# Revit family: ContinuousSpouting_RainwaterHead_Taper
name_source: partatom
category: Plumbing Fixtures
revit_build: Autodesk Revit 2013 (Build: 20121003_2115(x64)
units: mm (PartAtom-declared; Revit-internal decimal feet)

## types (5) — shared parameters
Base Depth = 155 mm  [stored 0.50853 ft]
Base Width = 200 mm  [stored 0.656168 ft]
Distance from Wall = 20 mm  [stored 0.0656168 ft]
Downpipe Offset = 100 mm  [stored 0.328084 ft]
Downpipe Radius = 40 mm  [stored 0.131234 ft]
Height = 300 mm  [stored 0.984252 ft]
Hole Radius = 39 mm  [stored 0.127953 ft]
Manufacturer = Continuous Group NZ Ltd
Model = Taper
Outlet Width = 140 mm  [stored 0.459318 ft]
Top Depth = 205 mm  [stored 0.672572 ft]
Top Width = 300 mm  [stored 0.984252 ft]
Type Comments = Rainwater Head
URL = http://www.continuous.co.nz

## per-type parameters (varying)
| type | Rainwater Head |
| Continuous Spouting - Taper (Copper) | CS-Copper |
| Continuous Spouting - Taper (Zinc) | CS-Zinc |
| Continuous Spouting - Taper (Aluminium) | CS-Aluminium |
| Continuous Spouting - Taper (Unpainted Zincalume) | CS-Unpainted Zincalume |
| Continuous Spouting - Taper (Colorcote®) | CS-Colorcote® |

note: [stored X ft] marks values corroborated as IEEE doubles in the binary element streams (Revit-internal decimal feet)

## geometry (parser evidence)
native form markers: Blend x14, Sweep x2
no freeform markers — native parametric forms only
